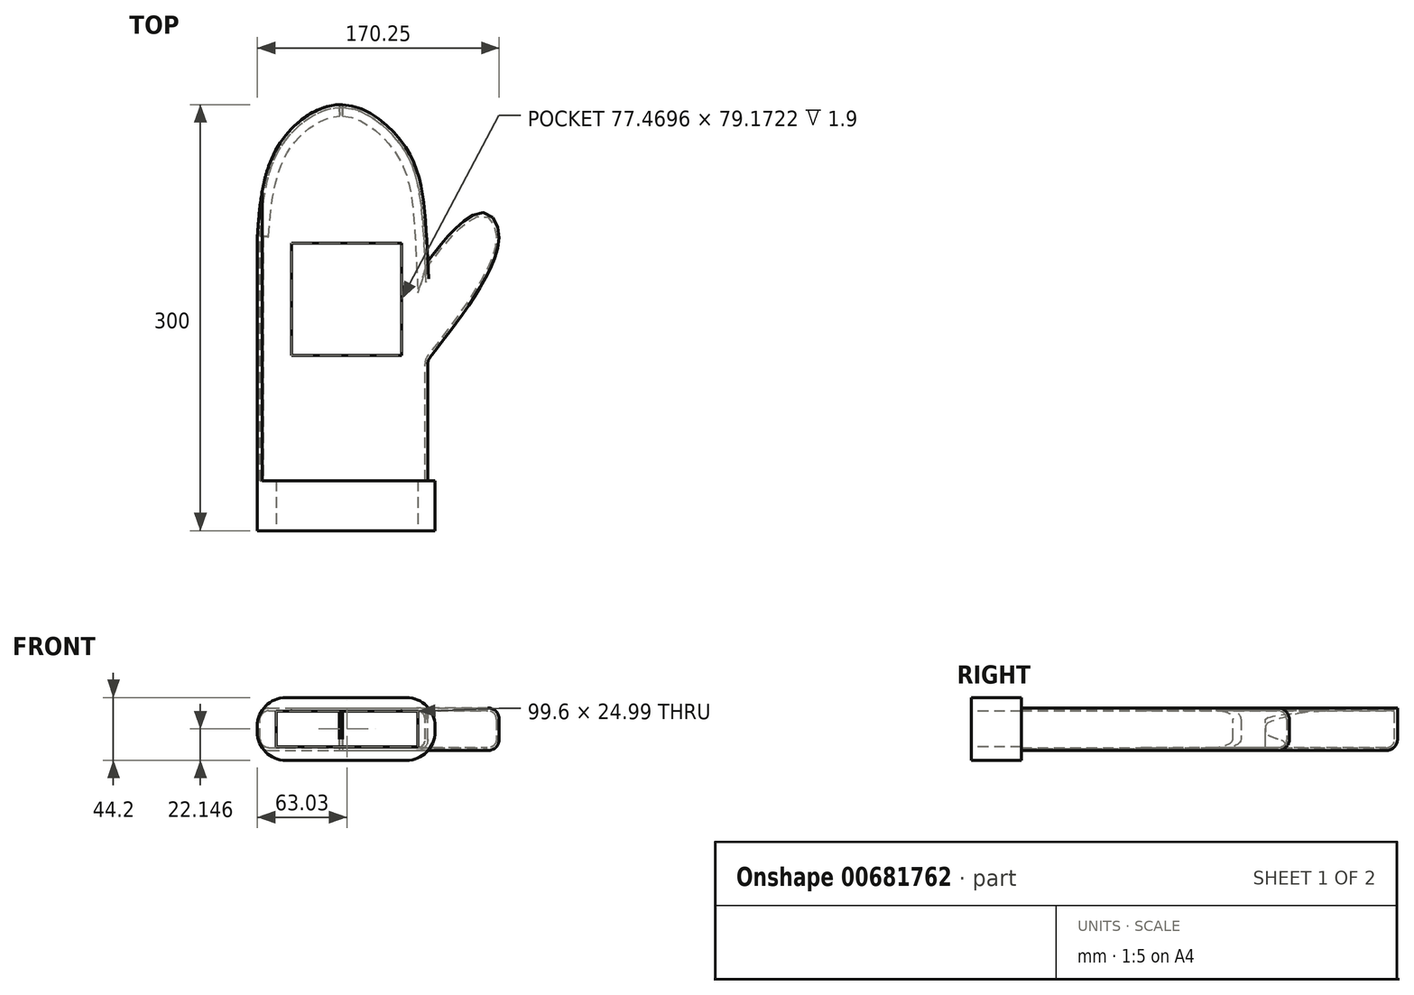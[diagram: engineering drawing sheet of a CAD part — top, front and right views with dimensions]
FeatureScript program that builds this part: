
annotation { "Feature Type Name" : "Feature", "Feature Type Description" : "" }
export const myFeature = defineFeature(function(context is Context, id is Id, definition is map)
    precondition{}
    {
        {
            var Q0;
            Q0=qCreatedBy(makeId("Top.planeOp"),FACE);
            var sketch = newSketch(context, id + "F0", { "sketchPlane" : qUnion([Q0])});
            skLineSegment(sketch, "E0.bottom", {"start": v(0, 0) * mm, "end": v(120, 0) * mm});
            skLineSegment(sketch, "E0.top", {"start": v(0, 300) * mm, "end": v(120, 300) * mm});
            skLineSegment(sketch, "E0.left", {"start": v(0, 0) * mm, "end": v(0, 300) * mm});
            skLineSegment(sketch, "E0.right", {"start": v(120, 0) * mm, "end": v(120, 300) * mm});
            skSolve(sketch);
        }
        {
            var Q0;
            Q0=qCreatedBy(makeId("Top.planeOp"),FACE);
            var sketch = newSketch(context, id + "F1", { "sketchPlane" : qUnion([Q0])});
            skFitSpline(sketch, "E1", {"points": [v(120, 120) * mm, v(170.25, 206.17) * mm, v(158.73, 223.93) * mm, v(120, 189.86) * mm], "startDerivative": vector(162.22, 209.62) * mm, "endDerivative": vector(-120.12, -158.28) * mm});
            skLineSegment(sketch, "E2", {"start": v(120, 189.86) * mm, "end": v(120, 120) * mm});
            skSolve(sketch);
        }
        {
            var Q0;
            Q0=makeQuery(id+"F0.imprint","IMPRINT",FACE,{"disambiguationData":[TD([[makeQuery(id+"F0.imprint","IMPRINT",EDGE,{"derivedFrom":sQuery(id+"F0.wireOp",EDGE,"E0.bottom")}),1.0]])]});
            extrude(context, id + "F2", {"entities" : qUnion([Q0]), "depth" : 30 * mm, "offsetDistance" : 25 * mm});
        }
        {
            var Q0;
            Q0=makeQuery(id+"F1.imprint","IMPRINT",FACE,{"disambiguationData":[TD([[makeQuery(id+"F1.imprint","IMPRINT",EDGE,{"derivedFrom":sQuery(id+"F1.wireOp",EDGE,"E1")}),1.0]])]});
            extrude(context, id + "F3", {"entities" : qUnion([Q0]), "operationType" : NewBodyOperationType.ADD, "depth" : 30 * mm, "offsetDistance" : 25 * mm});
        }
        {
            var Q0;
            Q0=makeQuery(id+"F3.boolean.opBoolean","MERGE",FACE,{"derivedFrom":[makeQuery(id+"F2.opExtrude","CAP_FACE",FACE,{"disambiguationData":[OSD([sQuery(id+"F0.wireOp",EDGE,"E0.bottom"),sQuery(id+"F0.wireOp",EDGE,"E0.top"),sQuery(id+"F0.wireOp",EDGE,"E0.left"),sQuery(id+"F0.wireOp",EDGE,"E0.right")])],"isStart":false}),makeQuery(id+"F3.opExtrude","CAP_FACE",FACE,{"disambiguationData":[OSD([sQuery(id+"F1.wireOp",EDGE,"E1"),sQuery(id+"F1.wireOp",EDGE,"E2")])],"isStart":false})]});
            var sketch = newSketch(context, id + "F4", { "sketchPlane" : qUnion([Q0])});
            skFitSpline(sketch, "E3", {"points": [v(0, 207.34) * mm, v(14.47, 270.55) * mm, v(60, 300) * mm, v(102.36, 272.96) * mm, v(116.1, 237.48) * mm, v(120, 189.86) * mm], "startDerivative": vector(22.35, 297.63) * mm, "endDerivative": vector(11.94, -256.22) * mm});
            skSolve(sketch);
        }
        {
            var Q0;
            {var subQ0=sQuery(id+"F4.wireOp",EDGE,"E3");var subQ1=makeQuery(id+"F2.opExtrude","CAP_EDGE",EDGE,{"disambiguationData":[OSD([sQuery(id+"F0.wireOp",EDGE,"E0.left")])],"isStart":false});var subQ2=makeQuery(id+"F4.imprint","INTERSECT",VERTEX,{"derivedFrom":[subQ1,subQ0]});Q0=makeQuery(id+"F4.imprint","IMPRINT",FACE,{"disambiguationData":[TD([[makeQuery(id+"F4.imprint","IMPRINT",EDGE,{"disambiguationData":[TD([[subQ2,-1.0]])],"derivedFrom":subQ0}),1.0]])]});}
            var Q1;
            {var subQ2=sQuery(id+"F0.wireOp",EDGE,"E0.right");var subQ3=sQuery(id+"F0.wireOp",EDGE,"E0.top");var subQ4=makeQuery(id+"F3.boolean.opBoolean","SPLIT",EDGE,{"disambiguationData":[TD([makeQuery(id+"F2.opExtrude","SWEPT_FACE",FACE,{"disambiguationData":[OSD([subQ3])]})])],"derivedFrom":makeQuery(id+"F2.opExtrude","CAP_EDGE",EDGE,{"disambiguationData":[OSD([subQ2])],"isStart":false})});Q1=makeQuery(id+"F4.imprint","IMPRINT",FACE,{"disambiguationData":[TD([[makeQuery(id+"F4.imprint","IMPRINT",EDGE,{"derivedFrom":subQ4}),1.0]])]});}
            extrude(context, id + "F5", {"entities" : qUnion([Q0, Q1]), "operationType" : NewBodyOperationType.REMOVE, "endBound" : BoundingType.THROUGH_ALL, "oppositeDirection" : true, "depth" : 25 * mm, "offsetDistance" : 25 * mm});
        }
        {
            var Q0;
            {var subQ0=sQuery(id+"F4.wireOp",EDGE,"E3");var subQ3=sQuery(id+"F0.wireOp",EDGE,"E0.top");Q0=makeQuery(id+"F5.boolean.opBoolean","COPY",EDGE,{"derivedFrom":makeQuery(id+"F5.opExtrude","CAP_EDGE",EDGE,{"disambiguationData":[OSD([subQ0]),TDD([makeQuery(id+"F4.imprint","IMPRINT",EDGE,{"disambiguationData":[TD([[makeQuery(id+"F4.imprint","INTERSECT",VERTEX,{"disambiguationData":[OD(1.0)],"derivedFrom":[makeQuery(id+"F2.opExtrude","CAP_EDGE",EDGE,{"disambiguationData":[OSD([subQ3])],"isStart":false}),subQ0]}),-1.0]])],"derivedFrom":subQ0})])],"isStart":true})});}
            var Q1;
            {var subQ0=sQuery(id+"F4.wireOp",EDGE,"E3");var subQ1=sQuery(id+"F1.wireOp",EDGE,"E1");var subQ2=sQuery(id+"F0.wireOp",EDGE,"E0.right");var subQ3=sQuery(id+"F0.wireOp",EDGE,"E0.top");var subQ4=sQuery(id+"F0.wireOp",EDGE,"E0.left");var subQ5=sQuery(id+"F0.wireOp",EDGE,"E0.bottom");var subQ6=sQuery(id+"F1.wireOp",EDGE,"E2");Q1=makeQuery(id+"F5.boolean.opBoolean","INTERSECT",EDGE,{"derivedFrom":[makeQuery(id+"F3.boolean.opBoolean","MERGE",FACE,{"derivedFrom":[makeQuery(id+"F2.opExtrude","CAP_FACE",FACE,{"disambiguationData":[OSD([subQ5,subQ3,subQ4,subQ2])],"isStart":true}),makeQuery(id+"F3.opExtrude","CAP_FACE",FACE,{"disambiguationData":[OSD([subQ1,subQ6])],"isStart":true})]}),makeQuery(id+"F5.opExtrude","SWEPT_FACE",FACE,{"disambiguationData":[OSD([subQ0]),TDD([makeQuery(id+"F4.imprint","IMPRINT",EDGE,{"disambiguationData":[TD([[makeQuery(id+"F4.imprint","INTERSECT",VERTEX,{"disambiguationData":[OD(1.0)],"derivedFrom":[makeQuery(id+"F2.opExtrude","CAP_EDGE",EDGE,{"disambiguationData":[OSD([subQ3])],"isStart":false}),subQ0]}),-1.0]])],"derivedFrom":subQ0})])]})]});}
            var Q2;
            {var subQ0=sQuery(id+"F4.wireOp",EDGE,"E3");var subQ1=sQuery(id+"F0.wireOp",EDGE,"E0.left");var subQ2=sQuery(id+"F0.wireOp",EDGE,"E0.top");Q2=makeQuery(id+"F5.boolean.opBoolean","INTERSECT",EDGE,{"derivedFrom":[makeQuery(id+"F3.boolean.opBoolean","MERGE",FACE,{"derivedFrom":[makeQuery(id+"F2.opExtrude","CAP_FACE",FACE,{"disambiguationData":[OSD([sQuery(id+"F0.wireOp",EDGE,"E0.bottom"),subQ2,subQ1,sQuery(id+"F0.wireOp",EDGE,"E0.right")])],"isStart":true}),makeQuery(id+"F3.opExtrude","CAP_FACE",FACE,{"disambiguationData":[OSD([sQuery(id+"F1.wireOp",EDGE,"E1"),sQuery(id+"F1.wireOp",EDGE,"E2")])],"isStart":true})]}),makeQuery(id+"F5.opExtrude","SWEPT_FACE",FACE,{"disambiguationData":[OSD([subQ0]),TDD([makeQuery(id+"F4.imprint","IMPRINT",EDGE,{"disambiguationData":[TD([[makeQuery(id+"F4.imprint","INTERSECT",VERTEX,{"derivedFrom":[makeQuery(id+"F2.opExtrude","CAP_EDGE",EDGE,{"disambiguationData":[OSD([subQ1])],"isStart":false}),subQ0]}),-1.0]])],"derivedFrom":subQ0})])]})]});}
            var Q3;
            {var subQ0=sQuery(id+"F4.wireOp",EDGE,"E3");Q3=makeQuery(id+"F5.boolean.opBoolean","COPY",EDGE,{"derivedFrom":makeQuery(id+"F5.opExtrude","CAP_EDGE",EDGE,{"disambiguationData":[OSD([subQ0]),TDD([makeQuery(id+"F4.imprint","IMPRINT",EDGE,{"disambiguationData":[TD([[makeQuery(id+"F4.imprint","INTERSECT",VERTEX,{"derivedFrom":[makeQuery(id+"F2.opExtrude","CAP_EDGE",EDGE,{"disambiguationData":[OSD([sQuery(id+"F0.wireOp",EDGE,"E0.left")])],"isStart":false}),subQ0]}),-1.0]])],"derivedFrom":subQ0})])],"isStart":true})});}
            var Q4;
            Q4=makeQuery(id+"F3.opExtrude","CAP_EDGE",EDGE,{"disambiguationData":[OSD([sQuery(id+"F1.wireOp",EDGE,"E1")])],"isStart":false});
            var Q5;
            Q5=makeQuery(id+"F3.opExtrude","CAP_EDGE",EDGE,{"disambiguationData":[OSD([sQuery(id+"F1.wireOp",EDGE,"E1")])],"isStart":true});
            var Q6;
            {var subQ1=sQuery(id+"F0.wireOp",EDGE,"E0.right");var subQ2=sQuery(id+"F0.wireOp",EDGE,"E0.bottom");Q6=makeQuery(id+"F3.boolean.opBoolean","SPLIT",EDGE,{"disambiguationData":[TD([makeQuery(id+"F2.opExtrude","SWEPT_FACE",FACE,{"disambiguationData":[OSD([subQ2])]})])],"derivedFrom":makeQuery(id+"F2.opExtrude","CAP_EDGE",EDGE,{"disambiguationData":[OSD([subQ1])],"isStart":false})});}
            var Q7;
            Q7=makeQuery(id+"F2.opExtrude","CAP_EDGE",EDGE,{"disambiguationData":[OSD([sQuery(id+"F0.wireOp",EDGE,"E0.left")])],"isStart":false});
            var Q8;
            Q8=makeQuery(id+"F2.opExtrude","CAP_EDGE",EDGE,{"disambiguationData":[OSD([sQuery(id+"F0.wireOp",EDGE,"E0.left")])],"isStart":true});
            var Q9;
            {var subQ0=sQuery(id+"F1.wireOp",EDGE,"E2");var subQ1=sQuery(id+"F1.wireOp",EDGE,"E1");Q9=makeQuery(id+"F3.opExtrude","SWEPT_EDGE",EDGE,{"disambiguationData":[OSD([subQ1,subQ0]),TDD([makeQuery(id+"F1.imprint","INTERSECT",VERTEX,{"disambiguationData":[OD(0.0)],"derivedFrom":[subQ1,subQ0]})])]});}
            var Q10;
            {var subQ1=sQuery(id+"F0.wireOp",EDGE,"E0.right");var subQ2=sQuery(id+"F0.wireOp",EDGE,"E0.bottom");Q10=makeQuery(id+"F3.boolean.opBoolean","SPLIT",EDGE,{"disambiguationData":[TD([makeQuery(id+"F2.opExtrude","SWEPT_FACE",FACE,{"disambiguationData":[OSD([subQ2])]})])],"derivedFrom":makeQuery(id+"F2.opExtrude","CAP_EDGE",EDGE,{"disambiguationData":[OSD([subQ1])],"isStart":true})});}
            fillet(context, id + "F6", {"entities" : qUnion([Q0, Q1, Q2, Q3, Q4, Q5, Q6, Q7, Q8, Q9, Q10]), "radius" : 8 * mm, "tangentPropagation" : true, "allowEdgeOverflow" : false});
        }
        {
            var Q0;
            Q0=makeQuery(id+"F2.opExtrude","SWEPT_FACE",FACE,{"disambiguationData":[OSD([sQuery(id+"F0.wireOp",EDGE,"E0.left")])]});
            var Q1;
            {var subQ0=sQuery(id+"F0.wireOp",EDGE,"E0.right");var subQ3=sQuery(id+"F0.wireOp",EDGE,"E0.bottom");Q1=makeQuery(id+"F3.boolean.opBoolean","SPLIT",FACE,{"disambiguationData":[TD([makeQuery(id+"F2.opExtrude","SWEPT_FACE",FACE,{"disambiguationData":[OSD([subQ3])]})])],"derivedFrom":makeQuery(id+"F2.opExtrude","SWEPT_FACE",FACE,{"disambiguationData":[OSD([subQ0])]})});}
            var Q2;
            {var subQ1=sQuery(id+"F0.wireOp",EDGE,"E0.right");var subQ2=sQuery(id+"F0.wireOp",EDGE,"E0.bottom");Q2=makeQuery(id+"F6.opFillet","BLEND_FACE",FACE,{"disambiguationData":[OSD([subQ1]),TDD([makeQuery(id+"F3.boolean.opBoolean","SPLIT",EDGE,{"disambiguationData":[TD([makeQuery(id+"F2.opExtrude","SWEPT_FACE",FACE,{"disambiguationData":[OSD([subQ2])]})])],"derivedFrom":makeQuery(id+"F2.opExtrude","CAP_EDGE",EDGE,{"disambiguationData":[OSD([subQ1])],"isStart":false})})])]});}
            var Q3;
            Q3=makeQuery(id+"F2.opExtrude","SWEPT_FACE",FACE,{"disambiguationData":[OSD([sQuery(id+"F0.wireOp",EDGE,"E0.bottom")])]});
            var Q4;
            {var subQ0=sQuery(id+"F0.wireOp",EDGE,"E0.left");Q4=makeQuery(id+"F6.opFillet","BLEND_FACE",FACE,{"disambiguationData":[OSD([subQ0]),TDD([makeQuery(id+"F2.opExtrude","CAP_EDGE",EDGE,{"disambiguationData":[OSD([subQ0])],"isStart":false})])]});}
            var Q5;
            {var subQ1=sQuery(id+"F0.wireOp",EDGE,"E0.right");var subQ2=sQuery(id+"F0.wireOp",EDGE,"E0.bottom");Q5=makeQuery(id+"F6.opFillet","BLEND_FACE",FACE,{"disambiguationData":[OSD([subQ1]),TDD([makeQuery(id+"F3.boolean.opBoolean","SPLIT",EDGE,{"disambiguationData":[TD([makeQuery(id+"F2.opExtrude","SWEPT_FACE",FACE,{"disambiguationData":[OSD([subQ2])]})])],"derivedFrom":makeQuery(id+"F2.opExtrude","CAP_EDGE",EDGE,{"disambiguationData":[OSD([subQ1])],"isStart":true})})])]});}
            var Q6;
            {var subQ0=sQuery(id+"F1.wireOp",EDGE,"E1");Q6=makeQuery(id+"F6.opFillet","BLEND_FACE",FACE,{"disambiguationData":[OSD([subQ0]),TDD([makeQuery(id+"F3.opExtrude","CAP_EDGE",EDGE,{"disambiguationData":[OSD([subQ0])],"isStart":true})])]});}
            var Q7;
            {var subQ0=sQuery(id+"F4.wireOp",EDGE,"E3");var subQ3=sQuery(id+"F0.wireOp",EDGE,"E0.top");Q7=makeQuery(id+"F6.opFillet","BLEND_FACE",FACE,{"disambiguationData":[OSD([subQ0]),TDD([makeQuery(id+"F5.boolean.opBoolean","COPY",EDGE,{"derivedFrom":makeQuery(id+"F5.opExtrude","CAP_EDGE",EDGE,{"disambiguationData":[OSD([subQ0]),TDD([makeQuery(id+"F4.imprint","IMPRINT",EDGE,{"disambiguationData":[TD([[makeQuery(id+"F4.imprint","INTERSECT",VERTEX,{"disambiguationData":[OD(1.0)],"derivedFrom":[makeQuery(id+"F2.opExtrude","CAP_EDGE",EDGE,{"disambiguationData":[OSD([subQ3])],"isStart":false}),subQ0]}),-1.0]])],"derivedFrom":subQ0})])],"isStart":true})})]),OD(0.0)]});}
            var Q8;
            {var subQ0=sQuery(id+"F4.wireOp",EDGE,"E3");Q8=makeQuery(id+"F6.opFillet","BLEND_FACE",FACE,{"disambiguationData":[OSD([subQ0]),TDD([makeQuery(id+"F5.boolean.opBoolean","COPY",EDGE,{"derivedFrom":makeQuery(id+"F5.opExtrude","CAP_EDGE",EDGE,{"disambiguationData":[OSD([subQ0]),TDD([makeQuery(id+"F4.imprint","IMPRINT",EDGE,{"disambiguationData":[TD([[makeQuery(id+"F4.imprint","INTERSECT",VERTEX,{"derivedFrom":[makeQuery(id+"F2.opExtrude","CAP_EDGE",EDGE,{"disambiguationData":[OSD([sQuery(id+"F0.wireOp",EDGE,"E0.left")])],"isStart":false}),subQ0]}),-1.0]])],"derivedFrom":subQ0})])],"isStart":true})})])]});}
            var Q9;
            {var subQ0=sQuery(id+"F0.wireOp",EDGE,"E0.left");Q9=makeQuery(id+"F6.opFillet","BLEND_FACE",FACE,{"disambiguationData":[OSD([subQ0]),TDD([makeQuery(id+"F2.opExtrude","CAP_EDGE",EDGE,{"disambiguationData":[OSD([subQ0])],"isStart":true})])]});}
            var Q10;
            {var subQ0=sQuery(id+"F1.wireOp",EDGE,"E1");Q10=makeQuery(id+"F6.opFillet","BLEND_FACE",FACE,{"disambiguationData":[OSD([subQ0]),TDD([makeQuery(id+"F3.opExtrude","CAP_EDGE",EDGE,{"disambiguationData":[OSD([subQ0])],"isStart":false})])]});}
            var Q11;
            {var subQ0=sQuery(id+"F4.wireOp",EDGE,"E3");var subQ3=sQuery(id+"F0.wireOp",EDGE,"E0.top");Q11=makeQuery(id+"F6.opFillet","BLEND_FACE",FACE,{"disambiguationData":[OSD([subQ0]),TDD([makeQuery(id+"F5.boolean.opBoolean","COPY",EDGE,{"derivedFrom":makeQuery(id+"F5.opExtrude","CAP_EDGE",EDGE,{"disambiguationData":[OSD([subQ0]),TDD([makeQuery(id+"F4.imprint","IMPRINT",EDGE,{"disambiguationData":[TD([[makeQuery(id+"F4.imprint","INTERSECT",VERTEX,{"disambiguationData":[OD(1.0)],"derivedFrom":[makeQuery(id+"F2.opExtrude","CAP_EDGE",EDGE,{"disambiguationData":[OSD([subQ3])],"isStart":false}),subQ0]}),-1.0]])],"derivedFrom":subQ0})])],"isStart":true})})]),OD(1.0)]});}
            var Q12;
            {var subQ0=sQuery(id+"F1.wireOp",EDGE,"E2");var subQ1=sQuery(id+"F1.wireOp",EDGE,"E1");Q12=makeQuery(id+"F6.opFillet","BLEND_FACE",FACE,{"disambiguationData":[OSD([subQ1,subQ0]),TDD([makeQuery(id+"F3.opExtrude","SWEPT_EDGE",EDGE,{"disambiguationData":[OSD([subQ1,subQ0]),TDD([makeQuery(id+"F1.imprint","INTERSECT",VERTEX,{"disambiguationData":[OD(0.0)],"derivedFrom":[subQ1,subQ0]})])]})])]});}
            var Q13;
            Q13=makeQuery(id+"F3.opExtrude","SWEPT_FACE",FACE,{"disambiguationData":[OSD([sQuery(id+"F1.wireOp",EDGE,"E1")])]});
            var Q14;
            Q14=makeQuery(id+"F3.boolean.opBoolean","MERGE",FACE,{"derivedFrom":[makeQuery(id+"F2.opExtrude","CAP_FACE",FACE,{"disambiguationData":[OSD([sQuery(id+"F0.wireOp",EDGE,"E0.bottom"),sQuery(id+"F0.wireOp",EDGE,"E0.top"),sQuery(id+"F0.wireOp",EDGE,"E0.left"),sQuery(id+"F0.wireOp",EDGE,"E0.right")])],"isStart":false}),makeQuery(id+"F3.opExtrude","CAP_FACE",FACE,{"disambiguationData":[OSD([sQuery(id+"F1.wireOp",EDGE,"E1"),sQuery(id+"F1.wireOp",EDGE,"E2")])],"isStart":false})]});
            var Q15;
            {var subQ0=sQuery(id+"F1.wireOp",EDGE,"E2");var subQ1=sQuery(id+"F1.wireOp",EDGE,"E1");Q15=makeQuery(id+"F6.opFillet","BLEND_FACE",FACE,{"disambiguationData":[OSD([subQ1,subQ0]),TDD([makeQuery(id+"F3.opExtrude","CAP_VERTEX",VERTEX,{"disambiguationData":[OSD([subQ1,subQ0]),TDD([makeQuery(id+"F1.imprint","INTERSECT",VERTEX,{"disambiguationData":[OD(0.0)],"derivedFrom":[subQ1,subQ0]})])],"isStart":true})])]});}
            var Q16;
            {var subQ0=sQuery(id+"F1.wireOp",EDGE,"E2");var subQ1=sQuery(id+"F1.wireOp",EDGE,"E1");Q16=makeQuery(id+"F6.opFillet","BLEND_FACE",FACE,{"disambiguationData":[OSD([subQ1,subQ0]),TDD([makeQuery(id+"F3.opExtrude","CAP_VERTEX",VERTEX,{"disambiguationData":[OSD([subQ1,subQ0]),TDD([makeQuery(id+"F1.imprint","INTERSECT",VERTEX,{"disambiguationData":[OD(0.0)],"derivedFrom":[subQ1,subQ0]})])],"isStart":false})])]});}
            var Q17;
            Q17=makeQuery(id+"F3.boolean.opBoolean","MERGE",FACE,{"derivedFrom":[makeQuery(id+"F2.opExtrude","CAP_FACE",FACE,{"disambiguationData":[OSD([sQuery(id+"F0.wireOp",EDGE,"E0.bottom"),sQuery(id+"F0.wireOp",EDGE,"E0.top"),sQuery(id+"F0.wireOp",EDGE,"E0.left"),sQuery(id+"F0.wireOp",EDGE,"E0.right")])],"isStart":true}),makeQuery(id+"F3.opExtrude","CAP_FACE",FACE,{"disambiguationData":[OSD([sQuery(id+"F1.wireOp",EDGE,"E1"),sQuery(id+"F1.wireOp",EDGE,"E2")])],"isStart":true})]});
            var Q18;
            {var subQ0=sQuery(id+"F4.wireOp",EDGE,"E3");var subQ1=sQuery(id+"F1.wireOp",EDGE,"E1");var subQ2=sQuery(id+"F0.wireOp",EDGE,"E0.right");var subQ3=sQuery(id+"F0.wireOp",EDGE,"E0.top");var subQ4=sQuery(id+"F0.wireOp",EDGE,"E0.left");var subQ5=sQuery(id+"F0.wireOp",EDGE,"E0.bottom");var subQ6=sQuery(id+"F1.wireOp",EDGE,"E2");Q18=makeQuery(id+"F6.opFillet","BLEND_FACE",FACE,{"disambiguationData":[OSD([subQ5,subQ3,subQ4,subQ2,subQ1,subQ6,subQ0]),TDD([makeQuery(id+"F5.boolean.opBoolean","INTERSECT",EDGE,{"derivedFrom":[makeQuery(id+"F3.boolean.opBoolean","MERGE",FACE,{"derivedFrom":[makeQuery(id+"F2.opExtrude","CAP_FACE",FACE,{"disambiguationData":[OSD([subQ5,subQ3,subQ4,subQ2])],"isStart":true}),makeQuery(id+"F3.opExtrude","CAP_FACE",FACE,{"disambiguationData":[OSD([subQ1,subQ6])],"isStart":true})]}),makeQuery(id+"F5.opExtrude","SWEPT_FACE",FACE,{"disambiguationData":[OSD([subQ0]),TDD([makeQuery(id+"F4.imprint","IMPRINT",EDGE,{"disambiguationData":[TD([[makeQuery(id+"F4.imprint","INTERSECT",VERTEX,{"disambiguationData":[OD(1.0)],"derivedFrom":[makeQuery(id+"F2.opExtrude","CAP_EDGE",EDGE,{"disambiguationData":[OSD([subQ3])],"isStart":false}),subQ0]}),-1.0]])],"derivedFrom":subQ0})])]})]})])]});}
            var Q19;
            {var subQ0=sQuery(id+"F4.wireOp",EDGE,"E3");var subQ3=sQuery(id+"F0.wireOp",EDGE,"E0.top");Q19=makeQuery(id+"F5.boolean.opBoolean","COPY",FACE,{"derivedFrom":makeQuery(id+"F5.opExtrude","SWEPT_FACE",FACE,{"disambiguationData":[OSD([subQ0]),TDD([makeQuery(id+"F4.imprint","IMPRINT",EDGE,{"disambiguationData":[TD([[makeQuery(id+"F4.imprint","INTERSECT",VERTEX,{"disambiguationData":[OD(1.0)],"derivedFrom":[makeQuery(id+"F2.opExtrude","CAP_EDGE",EDGE,{"disambiguationData":[OSD([subQ3])],"isStart":false}),subQ0]}),-1.0]])],"derivedFrom":subQ0})])]})});}
            var Q20;
            {var subQ0=sQuery(id+"F4.wireOp",EDGE,"E3");Q20=makeQuery(id+"F5.boolean.opBoolean","COPY",FACE,{"derivedFrom":makeQuery(id+"F5.opExtrude","SWEPT_FACE",FACE,{"disambiguationData":[OSD([subQ0]),TDD([makeQuery(id+"F4.imprint","IMPRINT",EDGE,{"disambiguationData":[TD([[makeQuery(id+"F4.imprint","INTERSECT",VERTEX,{"derivedFrom":[makeQuery(id+"F2.opExtrude","CAP_EDGE",EDGE,{"disambiguationData":[OSD([sQuery(id+"F0.wireOp",EDGE,"E0.left")])],"isStart":false}),subQ0]}),-1.0]])],"derivedFrom":subQ0})])]})});}
            var Q21;
            {var subQ0=sQuery(id+"F4.wireOp",EDGE,"E3");var subQ1=sQuery(id+"F0.wireOp",EDGE,"E0.left");var subQ2=sQuery(id+"F0.wireOp",EDGE,"E0.top");var subQ3=sQuery(id+"F1.wireOp",EDGE,"E2");var subQ4=sQuery(id+"F1.wireOp",EDGE,"E1");var subQ5=sQuery(id+"F0.wireOp",EDGE,"E0.right");var subQ6=sQuery(id+"F0.wireOp",EDGE,"E0.bottom");Q21=makeQuery(id+"F6.opFillet","BLEND_FACE",FACE,{"disambiguationData":[OSD([subQ6,subQ2,subQ1,subQ5,subQ4,subQ3,subQ0]),TDD([makeQuery(id+"F5.boolean.opBoolean","INTERSECT",EDGE,{"derivedFrom":[makeQuery(id+"F3.boolean.opBoolean","MERGE",FACE,{"derivedFrom":[makeQuery(id+"F2.opExtrude","CAP_FACE",FACE,{"disambiguationData":[OSD([subQ6,subQ2,subQ1,subQ5])],"isStart":true}),makeQuery(id+"F3.opExtrude","CAP_FACE",FACE,{"disambiguationData":[OSD([subQ4,subQ3])],"isStart":true})]}),makeQuery(id+"F5.opExtrude","SWEPT_FACE",FACE,{"disambiguationData":[OSD([subQ0]),TDD([makeQuery(id+"F4.imprint","IMPRINT",EDGE,{"disambiguationData":[TD([[makeQuery(id+"F4.imprint","INTERSECT",VERTEX,{"derivedFrom":[makeQuery(id+"F2.opExtrude","CAP_EDGE",EDGE,{"disambiguationData":[OSD([subQ1])],"isStart":false}),subQ0]}),-1.0]])],"derivedFrom":subQ0})])]})]})]),OD(0.0)]});}
            var Q22;
            Q22=makeQuery(id+"F2.opExtrude","SWEPT_FACE",FACE,{"disambiguationData":[OSD([sQuery(id+"F0.wireOp",EDGE,"E0.top")])]});
            var Q23;
            {var subQ0=sQuery(id+"F4.wireOp",EDGE,"E3");var subQ1=sQuery(id+"F0.wireOp",EDGE,"E0.left");var subQ2=sQuery(id+"F0.wireOp",EDGE,"E0.top");var subQ3=sQuery(id+"F1.wireOp",EDGE,"E2");var subQ4=sQuery(id+"F1.wireOp",EDGE,"E1");var subQ5=sQuery(id+"F0.wireOp",EDGE,"E0.right");var subQ6=sQuery(id+"F0.wireOp",EDGE,"E0.bottom");Q23=makeQuery(id+"F6.opFillet","BLEND_FACE",FACE,{"disambiguationData":[OSD([subQ6,subQ2,subQ1,subQ5,subQ4,subQ3,subQ0]),TDD([makeQuery(id+"F5.boolean.opBoolean","INTERSECT",EDGE,{"derivedFrom":[makeQuery(id+"F3.boolean.opBoolean","MERGE",FACE,{"derivedFrom":[makeQuery(id+"F2.opExtrude","CAP_FACE",FACE,{"disambiguationData":[OSD([subQ6,subQ2,subQ1,subQ5])],"isStart":true}),makeQuery(id+"F3.opExtrude","CAP_FACE",FACE,{"disambiguationData":[OSD([subQ4,subQ3])],"isStart":true})]}),makeQuery(id+"F5.opExtrude","SWEPT_FACE",FACE,{"disambiguationData":[OSD([subQ0]),TDD([makeQuery(id+"F4.imprint","IMPRINT",EDGE,{"disambiguationData":[TD([[makeQuery(id+"F4.imprint","INTERSECT",VERTEX,{"derivedFrom":[makeQuery(id+"F2.opExtrude","CAP_EDGE",EDGE,{"disambiguationData":[OSD([subQ1])],"isStart":false}),subQ0]}),-1.0]])],"derivedFrom":subQ0})])]})]})]),OD(1.0)]});}
            var Q24;
            Q24=makeQuery(id+"F2.opExtrude","SWEPT_BODY",BODY,{"disambiguationData":[OSD([sQuery(id+"F0.wireOp",EDGE,"E0.bottom"),sQuery(id+"F0.wireOp",EDGE,"E0.top"),sQuery(id+"F0.wireOp",EDGE,"E0.left"),sQuery(id+"F0.wireOp",EDGE,"E0.right")])]});
            shell(context, id + "F7", {"isHollow" : true, "entities" : qUnion([Q0, Q1, Q2, Q3, Q4, Q5, Q6, Q7, Q8, Q9, Q10, Q11, Q12, Q13, Q14, Q15, Q16, Q17, Q18, Q19, Q20, Q21, Q22, Q23]), "parts" : qUnion([Q24]), "thickness" : 2 * mm});
        }
        {
            var Q0;
            Q0=makeQuery(id+"F2.opExtrude","SWEPT_FACE",FACE,{"disambiguationData":[OSD([sQuery(id+"F0.wireOp",EDGE,"E0.bottom")])]});
            var sketch = newSketch(context, id + "F8", { "sketchPlane" : qUnion([Q0])});
            skLineSegment(sketch, "E4.bottom", {"start": v(6.03, 25.33) * mm, "end": v(114.04, 25.33) * mm});
            skLineSegment(sketch, "E4.top", {"start": v(6.03, 4.22) * mm, "end": v(114.04, 4.22) * mm});
            skLineSegment(sketch, "E4.left", {"start": v(6.03, 25.33) * mm, "end": v(6.03, 4.22) * mm});
            skLineSegment(sketch, "E4.right", {"start": v(114.04, 25.33) * mm, "end": v(114.04, 4.22) * mm});
            skSolve(sketch);
        }
        {
            var Q0;
            Q0=makeQuery(id+"F8.imprint","IMPRINT",FACE,{"disambiguationData":[TD([[makeQuery(id+"F8.imprint","IMPRINT",EDGE,{"derivedFrom":sQuery(id+"F8.wireOp",EDGE,"E4.bottom")}),-1.0]])]});
            extrude(context, id + "F9", {"entities" : qUnion([Q0]), "operationType" : NewBodyOperationType.REMOVE, "oppositeDirection" : true, "depth" : 162 * mm, "offsetDistance" : 25 * mm});
        }
        {
            var Q0;
            Q0=qCreatedBy(makeId("Front.planeOp"),FACE);
            var sketch = newSketch(context, id + "F10", { "sketchPlane" : qUnion([Q0])});
            skLineSegment(sketch, "E5.bottom", {"start": v(0, 37.3) * mm, "end": v(125, 37.3) * mm});
            skLineSegment(sketch, "E5.top", {"start": v(0, -6.9) * mm, "end": v(125, -6.9) * mm});
            skLineSegment(sketch, "E5.left", {"start": v(0, 37.3) * mm, "end": v(0, -6.9) * mm});
            skLineSegment(sketch, "E5.right", {"start": v(125, 37.3) * mm, "end": v(125, -6.9) * mm});
            skSolve(sketch);
        }
        {
            var Q0;
            Q0=makeQuery(id+"F10.imprint","IMPRINT",FACE,{"disambiguationData":[TD([[makeQuery(id+"F10.imprint","IMPRINT",EDGE,{"derivedFrom":sQuery(id+"F10.wireOp",EDGE,"E5.bottom")}),-1.0]])]});
            extrude(context, id + "F11", {"entities" : qUnion([Q0]), "operationType" : NewBodyOperationType.ADD, "oppositeDirection" : true, "depth" : 35.2 * mm, "offsetDistance" : 25 * mm});
        }
        {
            var Q0;
            Q0=makeQuery(id+"F11.opExtrude","SWEPT_EDGE",EDGE,{"disambiguationData":[OSD([sQuery(id+"F10.wireOp",EDGE,"E5.bottom"),sQuery(id+"F10.wireOp",EDGE,"E5.left")])]});
            var Q1;
            Q1=makeQuery(id+"F11.opExtrude","SWEPT_EDGE",EDGE,{"disambiguationData":[OSD([sQuery(id+"F10.wireOp",EDGE,"E5.bottom"),sQuery(id+"F10.wireOp",EDGE,"E5.right")])]});
            var Q2;
            Q2=makeQuery(id+"F11.opExtrude","SWEPT_EDGE",EDGE,{"disambiguationData":[OSD([sQuery(id+"F10.wireOp",EDGE,"E5.top"),sQuery(id+"F10.wireOp",EDGE,"E5.right")])]});
            var Q3;
            Q3=makeQuery(id+"F11.opExtrude","SWEPT_EDGE",EDGE,{"disambiguationData":[OSD([sQuery(id+"F10.wireOp",EDGE,"E5.top"),sQuery(id+"F10.wireOp",EDGE,"E5.left")])]});
            fillet(context, id + "F12", {"entities" : qUnion([Q0, Q1, Q2, Q3]), "radius" : 20 * mm, "tangentPropagation" : true, "allowEdgeOverflow" : false});
        }
        {
            var Q0;
            Q0=makeQuery(id+"F11.boolean.opBoolean","MERGE",FACE,{"derivedFrom":[makeQuery(id+"F2.opExtrude","SWEPT_FACE",FACE,{"disambiguationData":[OSD([sQuery(id+"F0.wireOp",EDGE,"E0.bottom")])]}),makeQuery(id+"F11.opExtrude","CAP_FACE",FACE,{"disambiguationData":[OSD([sQuery(id+"F10.wireOp",EDGE,"E5.bottom"),sQuery(id+"F10.wireOp",EDGE,"E5.top"),sQuery(id+"F10.wireOp",EDGE,"E5.left"),sQuery(id+"F10.wireOp",EDGE,"E5.right")])],"isStart":true})]});
            var sketch = newSketch(context, id + "F13", { "sketchPlane" : qUnion([Q0])});
            skLineSegment(sketch, "E6.bottom", {"start": v(13.23, 27.74) * mm, "end": v(112.83, 27.74) * mm});
            skLineSegment(sketch, "E6.top", {"start": v(13.23, 2.75) * mm, "end": v(112.83, 2.75) * mm});
            skLineSegment(sketch, "E6.left", {"start": v(13.23, 27.74) * mm, "end": v(13.23, 2.75) * mm});
            skLineSegment(sketch, "E6.right", {"start": v(112.83, 27.74) * mm, "end": v(112.83, 2.75) * mm});
            skSolve(sketch);
        }
        {
            var Q0;
            Q0=makeQuery(id+"F13.imprint","IMPRINT",FACE,{"disambiguationData":[TD([[makeQuery(id+"F13.imprint","IMPRINT",EDGE,{"derivedFrom":sQuery(id+"F13.wireOp",EDGE,"E6.bottom")}),-1.0]])]});
            extrude(context, id + "F14", {"entities" : qUnion([Q0]), "operationType" : NewBodyOperationType.REMOVE, "oppositeDirection" : true, "depth" : 97.2 * mm, "offsetDistance" : 25 * mm});
        }
        {
            var Q0;
            Q0=makeQuery(id+"F3.boolean.opBoolean","MERGE",FACE,{"derivedFrom":[makeQuery(id+"F2.opExtrude","CAP_FACE",FACE,{"disambiguationData":[OSD([sQuery(id+"F0.wireOp",EDGE,"E0.bottom"),sQuery(id+"F0.wireOp",EDGE,"E0.top"),sQuery(id+"F0.wireOp",EDGE,"E0.left"),sQuery(id+"F0.wireOp",EDGE,"E0.right")])],"isStart":false}),makeQuery(id+"F3.opExtrude","CAP_FACE",FACE,{"disambiguationData":[OSD([sQuery(id+"F1.wireOp",EDGE,"E1"),sQuery(id+"F1.wireOp",EDGE,"E2")])],"isStart":false})]});
            var sketch = newSketch(context, id + "F15", { "sketchPlane" : qUnion([Q0])});
            skLineSegment(sketch, "E7.bottom", {"start": v(24.11, 202.58) * mm, "end": v(101.58, 202.58) * mm});
            skLineSegment(sketch, "E7.top", {"start": v(24.11, 123.4) * mm, "end": v(101.58, 123.4) * mm});
            skLineSegment(sketch, "E7.left", {"start": v(24.11, 202.58) * mm, "end": v(24.11, 123.4) * mm});
            skLineSegment(sketch, "E7.right", {"start": v(101.58, 202.58) * mm, "end": v(101.58, 123.4) * mm});
            skSolve(sketch);
        }
        {
            var Q0;
            Q0=makeQuery(id+"F15.imprint","IMPRINT",FACE,{"disambiguationData":[TD([[makeQuery(id+"F15.imprint","IMPRINT",EDGE,{"derivedFrom":sQuery(id+"F15.wireOp",EDGE,"E7.bottom")}),-1.0]])]});
            extrude(context, id + "F16", {"entities" : qUnion([Q0]), "operationType" : NewBodyOperationType.REMOVE, "oppositeDirection" : true, "depth" : 1.9 * mm, "offsetDistance" : 25 * mm});
        }
    });
